# Revit family: 29002-presto
name_source: partatom
category: Plumbing Fixtures
units: mm (PartAtom-declared; Revit-internal decimal feet)

## family parameters
Always vertical = Yes
Cut with Voids When Loaded = No
Maintain Annotation Orientation = No
OmniClass Number = 23.45.00.00
OmniClass Title = Sanitary, Laundry, and Cleaning Equipment
Part Type = Normal
Room Calculation Point = No
Round Connector Dimension = Use Diameter
Shared = No
Work Plane-Based = Yes

## types (1)
- 29002- Les Robinets PRESTO
    - Hydraulic supply = 20.00 mm
    > Standards & approvals = 200-hour neutral salt spray resistant (NSS) in accordance with ISO 9227 Brass body in accordance with EN 1982, EN 12164, EN 12156
50 l/min
3/4”
75°C
3 YEARS
PRESTO (LES ROBINETS) : Siège Social: 7 rue Racine 92542 Montrouge Cedex - Site de Production: 4 rue Lavoisier 17110 St-Georges de Didonne - Tel: 01.46.12.34.56 - Fax: 01.40.92.00.12 - www.presto.fr
R
R
A
A
N
T
W
Y
Y
W

200-hour neutral salt spray resistant (NSS) in accordance with ISO 9227 Brass body in accordance with EN 1982, EN 12164, EN 12156
50 l/min
3/4”
75°C
3 YEARS
PRESTO (LES ROBINETS) : Siège Social: 7 rue Racine 92542 Montrouge Cedex - Site de Production: 4 rue Lavoisier 17110 St-Georges de Didonne - Tel: 01.46.12.34.56 - Fax: 01.40.92.00.12 - www.presto.fr
R
R
A
A
N
T
W
Y
Y
W
200-hour neutral salt spray resistant (NSS) in accordance with ISO 9227 Brass body in accordance with EN 1982, EN 12164, EN 12156
    Assembly Code = 29002
    Default Elevation = 1219 mm
    Description = 29002 - Thermostatic mixing valve with disconnectable temperature control
    Minimum differential temperature = 15 °C
    Model = 29002 - Thermostatic mixing valve with temperature locking
    Recommended pressure = 3.0 Pa
    Stability of mixed water temperature = 2 °C
    URL = https://www.prestodatashare.com
    brand = Les Robinets PRESTO
    flow = 57.0 L/min
    material = <By Category>
    material 1 = green paint
    material 2 = croom
    min pressure = 1.0 Pa
    pressure = 5.0 Pa
    range = Safety Thermostatic Mixing Valve
    ref = 29002 - Thermostatic mixing valve with disconnectable temperature control
    temperature = 65 °C
    temperature hot wotar = 85 °C

## geometry (parser evidence)
native form markers: Sweep x3
no freeform markers — native parametric forms only
